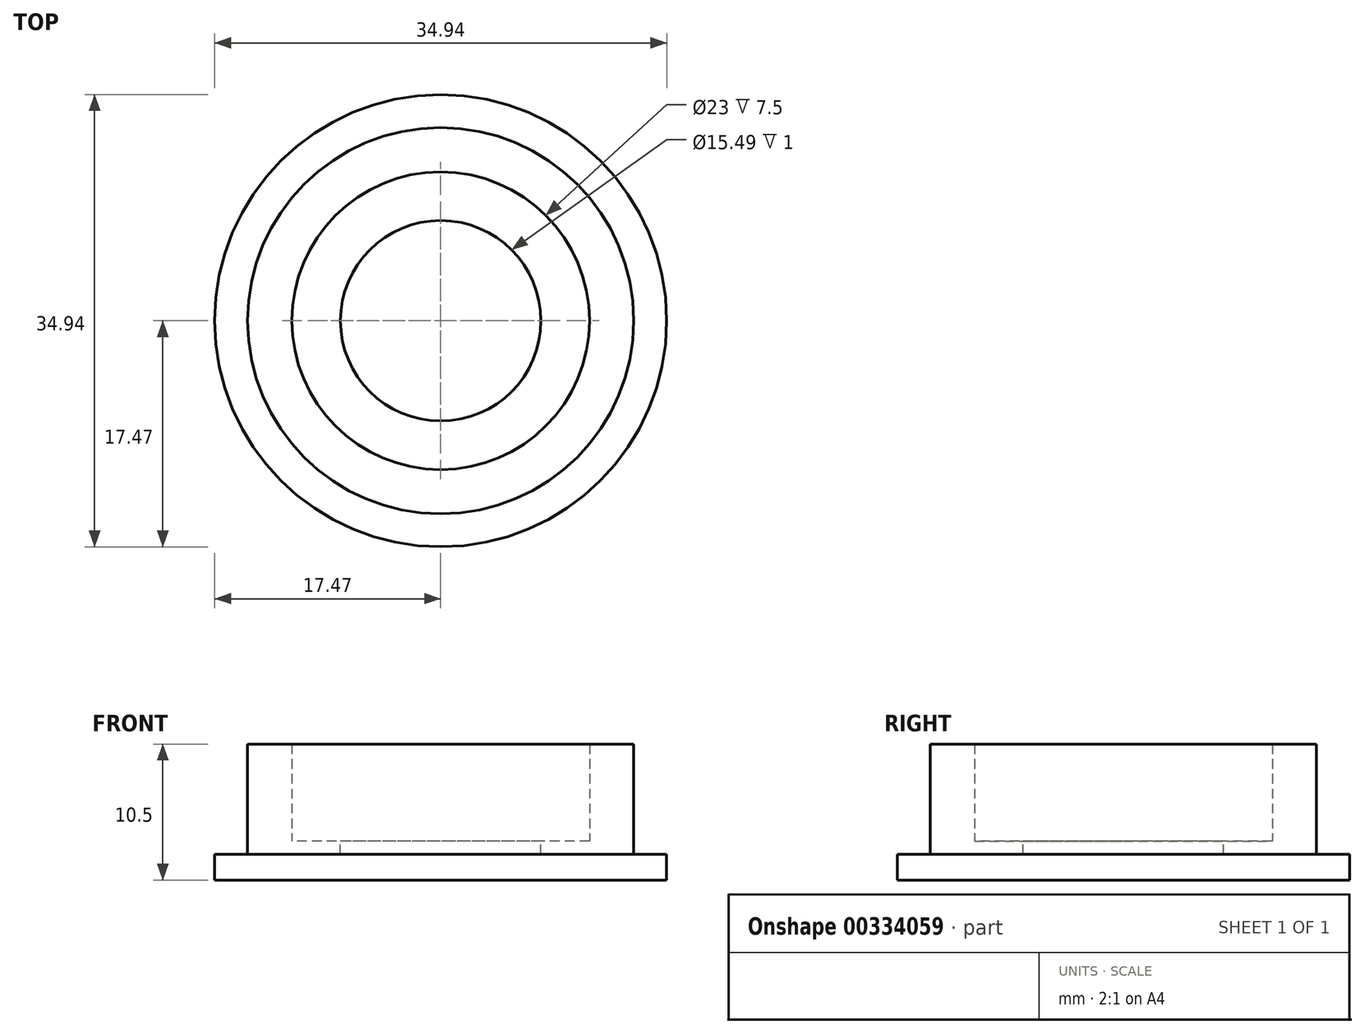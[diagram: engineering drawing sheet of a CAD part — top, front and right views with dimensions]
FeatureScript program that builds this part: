
annotation { "Feature Type Name" : "Feature", "Feature Type Description" : "" }
export const myFeature = defineFeature(function(context is Context, id is Id, definition is map)
    precondition{}
    {
        {
            var Q0;
            Q0=qCreatedBy(makeId("Top.planeOp"),FACE);
            var sketch = newSketch(context, id + "F0", { "sketchPlane" : qUnion([Q0])});
            skCircle(sketch, "E0", {"center": v(0, 0) * mm, "radius": 11.5 * mm});
            skCircle(sketch, "E1", {"center": v(0, 0) * mm, "radius": 14.92 * mm});
            skCircle(sketch, "E2", {"center": v(0, 0) * mm, "radius": 7.75 * mm});
            skSolve(sketch);
        }
        {
            var Q0;
            Q0 = qSketchRegion(id + "F0", true);
            extrude(context, id + "F1", {"entities" : qUnion([Q0]), "depth" : 8.5 * mm});
        }
        {
            var Q0;
            Q0=qCreatedBy(makeId("Top.planeOp"),FACE);
            var sketch = newSketch(context, id + "F2", { "sketchPlane" : qUnion([Q0])});
            skCircle(sketch, "E3", {"center": v(0, 0) * mm, "radius": 14.92 * mm});
            skSolve(sketch);
        }
        {
            var Q0;
            Q0 = qSketchRegion(id + "F2", true);
            extrude(context, id + "F3", {"entities" : qUnion([Q0]), "operationType" : NewBodyOperationType.ADD, "endBound" : BoundingType.SYMMETRIC, "oppositeDirection" : true, "depth" : 2 * mm});
        }
        {
            var Q0;
            Q0=makeQuery(id+"F3.opExtrude","CAP_FACE",FACE,{"disambiguationData":[OSD([sQuery(id+"F2.wireOp",EDGE,"E3")])],"isStart":true});
            var sketch = newSketch(context, id + "F4", { "sketchPlane" : qUnion([Q0])});
            skCircle(sketch, "E4", {"center": v(0, 0) * mm, "radius": 7.75 * mm});
            skSolve(sketch);
        }
        {
            var Q0;
            Q0 = qSketchRegion(id + "F4", true);
            var Q1;
            Q1=makeQuery(id+"F3.opExtrude","CAP_FACE",FACE,{"disambiguationData":[OSD([sQuery(id+"F2.wireOp",EDGE,"E3")])],"isStart":false});
            extrude(context, id + "F5", {"entities" : qUnion([Q0, Q1]), "operationType" : NewBodyOperationType.REMOVE, "oppositeDirection" : true, "depth" : 1 * mm});
        }
        {
            var Q0;
            Q0=makeQuery(id+"F3.opExtrude","CAP_FACE",FACE,{"disambiguationData":[OSD([sQuery(id+"F2.wireOp",EDGE,"E3")])],"isStart":false});
            extrude(context, id + "F6", {"entities" : qUnion([Q0]), "operationType" : NewBodyOperationType.ADD, "depth" : 1 * mm});
        }
        {
            var Q0;
            Q0=makeQuery(id+"F0.imprint","IMPRINT",FACE,{"disambiguationData":[TD([[makeQuery(id+"F0.imprint","IMPRINT",EDGE,{"derivedFrom":sQuery(id+"F0.wireOp",EDGE,"E2")}),1.0]])]});
            var sketch = newSketch(context, id + "F7", { "sketchPlane" : qUnion([Q0])});
            skCircle(sketch, "E5", {"center": v(0, 0) * mm, "radius": 17.47 * mm});
            skSolve(sketch);
        }
        {
            var Q0;
            Q0 = qSketchRegion(id + "F7", true);
            extrude(context, id + "F8", {"entities" : qUnion([Q0]), "operationType" : NewBodyOperationType.ADD, "oppositeDirection" : true, "depth" : 2 * mm});
        }
    });
